# Revit family: Maxlogic  Conventionnelle Panneau d'Alarme Incendie petite caisse
name_source: partatom
category: Fire Alarm Devices
units: mm (PartAtom-declared; Revit-internal decimal feet)

## family parameters
Cut with Voids When Loaded = No
Host = Face
Maintain Annotation Orientation = Yes
OmniClass Number = 23.85.30.21
OmniClass Title = Environmental Detection/Registration
Part Type = Normal
Room Calculation Point = No
Round Connector Dimension = Use Diameter
Shared = No

## types (3) — shared parameters
Adresse ligne 1 = Şerifali Mahallesi Kutup Sokak No:27/1-2-4 Ümraniye TR-34775 İSTANBUL
Alimentation d'externe = 220 V AC
Batterie = 2 X (12V DC 2,1 Ah )
Code de  Performance = EN 54-2 / EN 54-4
Couleur = Blanc
Deuxime Matèriel = Plastique Blanche ABS
Durée de la garantie Travail = 2
Durée de la garantie réservé = 2
Hauteur Nominale = 240 mm
Largeur Nominale = 90 mm
Longeur Nominale = 320 mm
Manuel d'installation = https://mavilielektronik.com
Manufacturer = Mavili Elektronik Ticaret A.Ş.
Matériel Principe = Mètale Grise
Model = Maxlogic
Numèro de Fax = (+)90 216 466 45 10
Poids = 3450 gr
Surface de Montage = Montage à Mur
Tempèrature de Fonctionnement = (-5°C) - (+40°C)
URL = https://www.mavili.com.tr
Unité de durée de garantie = Ans
protection de Classe = IP 30
zero-valued in all types: Cost, Default Elevation

## per-type parameters (varying)
| type | 2 led | 4 led | Code de Produit | Description |
| Maxlogic Panneau Contrôle d'Incendie Conventionnelle, 2 Zone | No | No | ML-2222 | Panneau Contrôle d'Incendie Conventionnelle, 2 Zone |
| Maxlogic Panneau Contrôle d'Incendie Conventionnelle, 4 Zone | Yes | No | ML-2224 | Panneau Contrôle d'Incendie Conventionnelle, 4 Zone |
| Maxlogic Panneau Contrôle d'Incendie Conventionnelle, 8 Zone | Yes | Yes | ML-2228 | Panneau Contrôle d'Incendie Conventionnelle, 8 Zone |

## geometry (parser evidence)
native form markers: Sweep x2
no freeform markers — native parametric forms only
